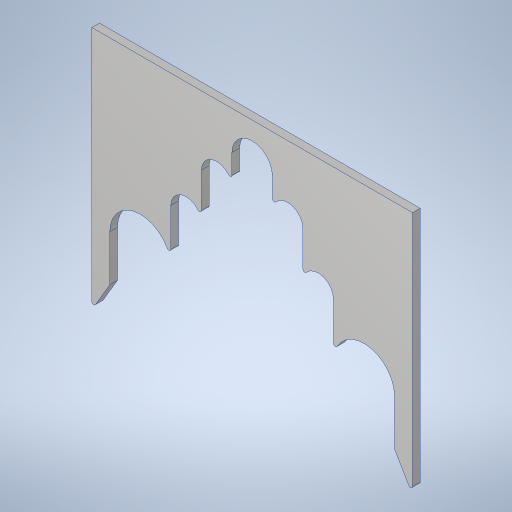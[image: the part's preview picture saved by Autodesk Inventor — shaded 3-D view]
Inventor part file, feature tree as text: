
AUTODESK INVENTOR PART (.ipt)
format: ipt  version: 2023.4 (Build 274418000, 418)  size: 290,816 bytes
history: native  units: in
note: dims shown in document units (in); Inventor stores cm internally (conversion verified against a paired STEP export)
features: extrude x1, fillet x1, sketch x1
ambient origin geometry x8: Origin, YZ Plane, XZ Plane, XY Plane, X Axis, Y Axis, Z Axis, Center Point
bodies: Solid1 (feature_tree)
feature tree (3):
  extrude  "Extrusion1"  Depth=0.0625in
  fillet  "Fillet1"  Radius=0.5in
  sketch  "Sketch1"  dims[d0=10.5in d1=8.0in d3=0.5in d4=0.5in d5=1.0in d7=1.325in d8=90.0deg d9=90.0deg d10=90.0deg d11=1.0in d12=90.0deg d13=1.75in d14=1.75in d15=1.0in d16=1.0in d17=1.5in d18=1.5in d19=1.0in d21=2.0in d22=2.0in d23=1.25in d25=0.25in d26=0.0in d27=0.0625in]
